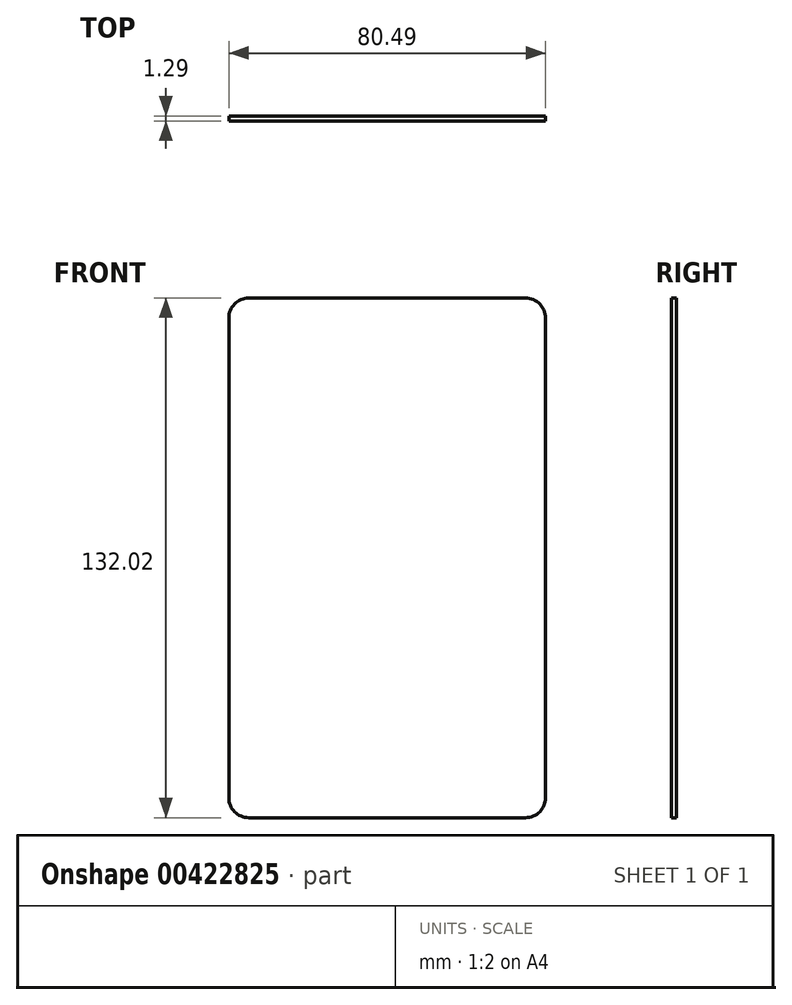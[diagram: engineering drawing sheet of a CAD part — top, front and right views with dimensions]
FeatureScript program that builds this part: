
annotation { "Feature Type Name" : "Feature", "Feature Type Description" : "" }
export const myFeature = defineFeature(function(context is Context, id is Id, definition is map)
    precondition{}
    {
        {
            var Q0;
            Q0=qCreatedBy(makeId("Front.planeOp"),FACE);
            var sketch = newSketch(context, id + "F0", { "sketchPlane" : qUnion([Q0])});
            skLineSegment(sketch, "E0.bottom", {"start": v(-34.21, 60.5) * mm, "end": v(46.28, 60.5) * mm});
            skLineSegment(sketch, "E0.top", {"start": v(-34.21, -71.53) * mm, "end": v(46.28, -71.53) * mm});
            skLineSegment(sketch, "E0.left", {"start": v(-34.21, 60.5) * mm, "end": v(-34.21, -71.53) * mm});
            skLineSegment(sketch, "E0.right", {"start": v(46.28, 60.5) * mm, "end": v(46.28, -71.53) * mm});
            skSolve(sketch);
        }
        {
            var Q0;
            Q0=makeQuery(id+"F0.imprint","IMPRINT",FACE,{"disambiguationData":[TD([[makeQuery(id+"F0.imprint","IMPRINT",EDGE,{"derivedFrom":sQuery(id+"F0.wireOp",EDGE,"E0.bottom")}),-1.0]])]});
            extrude(context, id + "F1", {"entities" : qUnion([Q0]), "depth" : 1.3 * mm});
        }
        {
            var Q0;
            Q0=makeQuery(id+"F1.opExtrude","SWEPT_EDGE",EDGE,{"disambiguationData":[OSD([sQuery(id+"F0.wireOp",EDGE,"E0.top"),sQuery(id+"F0.wireOp",EDGE,"E0.left")])]});
            fillet(context, id + "F2", {"entities" : qUnion([Q0]), "radius" : 5.08 * mm, "tangentPropagation" : true, "allowEdgeOverflow" : false});
        }
        {
            var Q0;
            Q0=makeQuery(id+"F1.opExtrude","SWEPT_EDGE",EDGE,{"disambiguationData":[OSD([sQuery(id+"F0.wireOp",EDGE,"E0.top"),sQuery(id+"F0.wireOp",EDGE,"E0.right")])]});
            fillet(context, id + "F3", {"entities" : qUnion([Q0]), "radius" : 5.08 * mm, "tangentPropagation" : true, "allowEdgeOverflow" : false});
        }
        {
            var Q0;
            Q0=makeQuery(id+"F1.opExtrude","SWEPT_EDGE",EDGE,{"disambiguationData":[OSD([sQuery(id+"F0.wireOp",EDGE,"E0.bottom"),sQuery(id+"F0.wireOp",EDGE,"E0.right")])]});
            fillet(context, id + "F4", {"entities" : qUnion([Q0]), "radius" : 5.08 * mm, "tangentPropagation" : true, "allowEdgeOverflow" : false});
        }
        {
            var Q0;
            Q0=makeQuery(id+"F1.opExtrude","SWEPT_EDGE",EDGE,{"disambiguationData":[OSD([sQuery(id+"F0.wireOp",EDGE,"E0.bottom"),sQuery(id+"F0.wireOp",EDGE,"E0.left")])]});
            fillet(context, id + "F5", {"entities" : qUnion([Q0]), "radius" : 5.08 * mm, "tangentPropagation" : true, "allowEdgeOverflow" : false});
        }
    });
